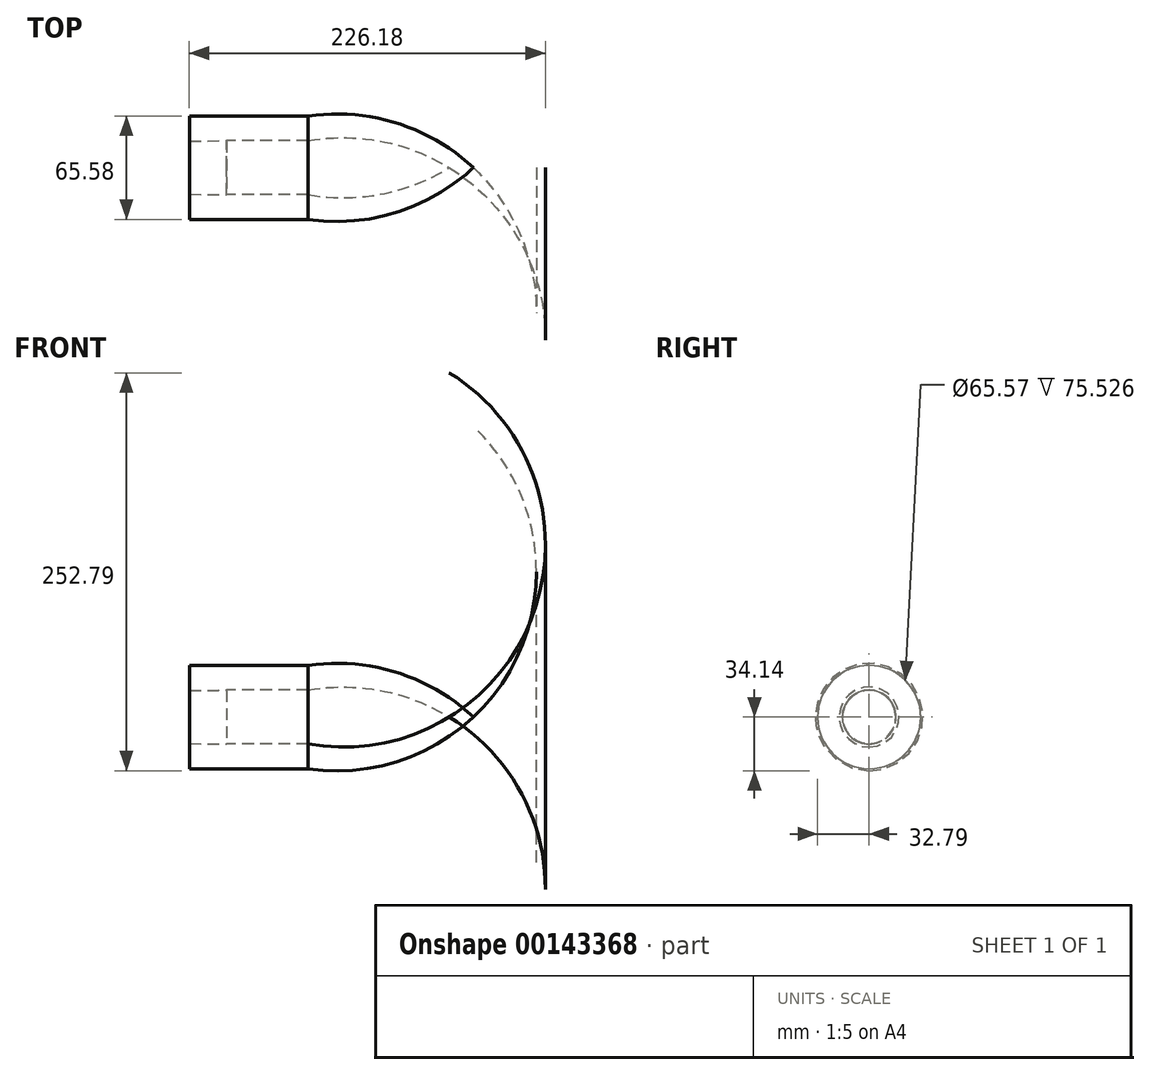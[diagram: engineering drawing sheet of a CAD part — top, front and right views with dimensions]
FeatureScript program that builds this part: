
annotation { "Feature Type Name" : "Feature", "Feature Type Description" : "" }
export const myFeature = defineFeature(function(context is Context, id is Id, definition is map)
    precondition{}
    {
        {
            var Q0;
            Q0=qCreatedBy(makeId("Front.planeOp"),FACE);
            var sketch = newSketch(context, id + "F0", { "sketchPlane" : qUnion([Q0])});
            skArc(sketch, "E0", {"start": v(89.59, 0) * mm, "mid": v(46.37, 16.8) * mm, "end": v(0, 17.14) * mm});
            skLineSegment(sketch, "E1", {"start": v(0, 32.79) * mm, "end": v(0, 17.14) * mm});
            skArc(sketch, "E2", {"start": v(104.87, 0) * mm, "mid": v(56.18, 28.38) * mm, "end": v(0, 32.79) * mm});
            skLineSegment(sketch, "E3", {"start": v(104.87, 0) * mm, "end": v(89.59, 0) * mm});
            skLineSegment(sketch, "E4", {"start": v(0, 0) * mm, "end": v(75.56, 0) * mm});
            skLineSegment(sketch, "E5", {"start": v(0, 32.79) * mm, "end": v(-51.88, 32.79) * mm});
            skLineSegment(sketch, "E6", {"start": v(-51.88, 32.79) * mm, "end": v(-51.88, 17.14) * mm});
            skLineSegment(sketch, "E7", {"start": v(-51.88, 17.14) * mm, "end": v(0, 17.14) * mm});
            skLineSegment(sketch, "E8", {"start": v(-51.88, 32.79) * mm, "end": v(-75.53, 32.79) * mm});
            skLineSegment(sketch, "E9", {"start": v(-75.53, 32.79) * mm, "end": v(-75.53, 16.87) * mm});
            skLineSegment(sketch, "E10", {"start": v(-75.53, 16.87) * mm, "end": v(-51.88, 17.14) * mm});
            skSolve(sketch);
        }
        {
            var Q0;
            Q0 = qSketchRegion(id + "F0", true);
            var Q1;
            Q1=sQuery(id+"F0.wireOp",EDGE,"E4");
            revolve(context, id + "F1", {"entities" : qUnion([Q0]), "axis" : qUnion([Q1]), "revolveType" : RevolveType.FULL});
        }
    });
